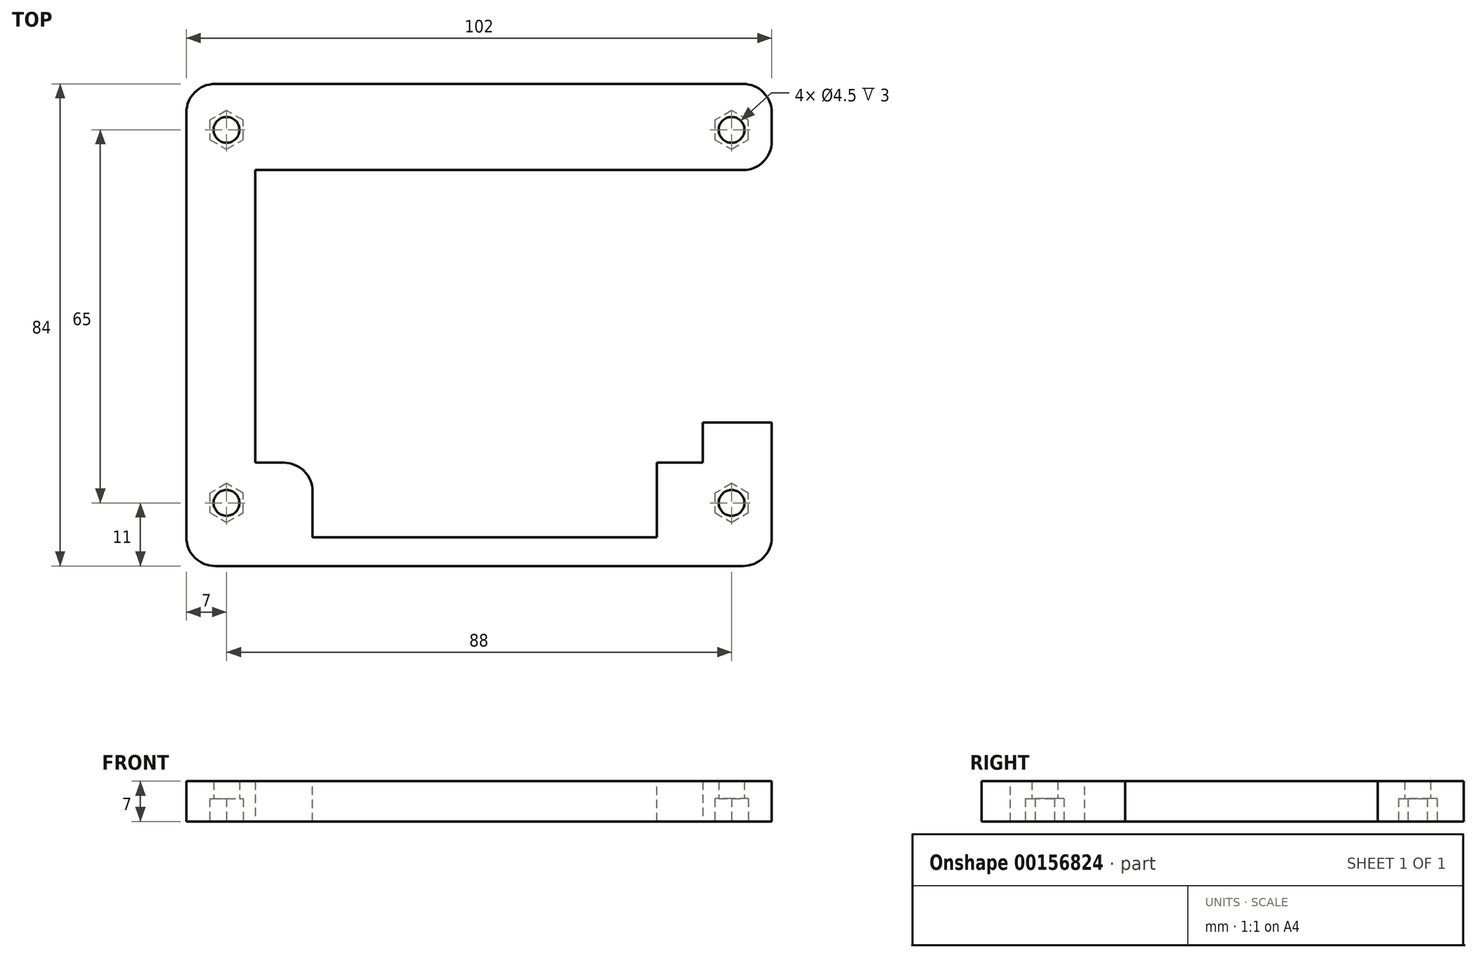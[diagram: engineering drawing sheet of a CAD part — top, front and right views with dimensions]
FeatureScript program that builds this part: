
annotation { "Feature Type Name" : "Feature", "Feature Type Description" : "" }
export const myFeature = defineFeature(function(context is Context, id is Id, definition is map)
    precondition{}
    {
        {
            var Q0;
            Q0=qCreatedBy(makeId("Top.planeOp"),FACE);
            var sketch = newSketch(context, id + "F0", { "sketchPlane" : qUnion([Q0])});
            skLineSegment(sketch, "E0.rect.bottom", {"start": v(44, -32.5) * mm, "end": v(-44, -32.5) * mm, "construction": true});
            skLineSegment(sketch, "E0.rect.top", {"start": v(44, 32.5) * mm, "end": v(-44, 32.5) * mm, "construction": true});
            skLineSegment(sketch, "E0.rect.left", {"start": v(44, -32.5) * mm, "end": v(44, 32.5) * mm, "construction": true});
            skLineSegment(sketch, "E0.rect.right", {"start": v(-44, -32.5) * mm, "end": v(-44, 32.5) * mm, "construction": true});
            skPoint(sketch, "E0.rect.middle", {"position": v(0, 0) * mm});
            skCircle(sketch, "E1", {"center": v(-44, 32.5) * mm, "radius": 2.25 * mm});
            skCircle(sketch, "E2", {"center": v(44, 32.5) * mm, "radius": 2.25 * mm});
            skCircle(sketch, "E3", {"center": v(-44, -32.5) * mm, "radius": 2.25 * mm});
            skCircle(sketch, "E4", {"center": v(44, -32.5) * mm, "radius": 2.25 * mm});
            skLineSegment(sketch, "E5.rect.bottom", {"start": v(39, -25.5) * mm, "end": v(-39, -25.5) * mm});
            skLineSegment(sketch, "E5.rect.top", {"start": v(39, 25.5) * mm, "end": v(-39, 25.5) * mm});
            skLineSegment(sketch, "E5.rect.left", {"start": v(39, -25.5) * mm, "end": v(39, 25.5) * mm});
            skLineSegment(sketch, "E5.rect.right", {"start": v(-39, -25.5) * mm, "end": v(-39, 25.5) * mm});
            skLineSegment(sketch, "E6", {"start": v(-51, -43.5) * mm, "end": v(51, -43.5) * mm});
            skLineSegment(sketch, "E7", {"start": v(51, -43.5) * mm, "end": v(51, 40.5) * mm});
            skLineSegment(sketch, "E8", {"start": v(51, 40.5) * mm, "end": v(-51, 40.5) * mm});
            skLineSegment(sketch, "E9", {"start": v(-51, 40.5) * mm, "end": v(-51, -43.5) * mm});
            skSolve(sketch);
        }
        {
            var Q0;
            Q0=qSketchRegion(id+"F0",true);
            extrude(context, id + "F1", {"entities" : qUnion([Q0]), "depth" : 15 * mm});
        }
        {
            var Q0;
            Q0=makeQuery(id+"F1.opExtrude","CAP_FACE",FACE,{"disambiguationData":[OSD([sQuery(id+"F0.wireOp",EDGE,"E1"),sQuery(id+"F0.wireOp",EDGE,"E2"),sQuery(id+"F0.wireOp",EDGE,"E3"),sQuery(id+"F0.wireOp",EDGE,"E4"),sQuery(id+"F0.wireOp",EDGE,"E5.rect.bottom"),sQuery(id+"F0.wireOp",EDGE,"E5.rect.top"),sQuery(id+"F0.wireOp",EDGE,"E5.rect.left"),sQuery(id+"F0.wireOp",EDGE,"E5.rect.right"),sQuery(id+"F0.wireOp",EDGE,"E6"),sQuery(id+"F0.wireOp",EDGE,"E7"),sQuery(id+"F0.wireOp",EDGE,"E8"),sQuery(id+"F0.wireOp",EDGE,"E9")])],"isStart":true});
            var sketch = newSketch(context, id + "F2", { "sketchPlane" : qUnion([Q0])});
            skCircle(sketch, "E10.cCircle", {"center": v(-44, 32.5) * mm, "radius": 2.92 * mm, "construction": true});
            skLineSegment(sketch, "E10.0", {"start": v(-41.08, 34.19) * mm, "end": v(-41.08, 30.81) * mm});
            skLineSegment(sketch, "E10.1", {"start": v(-41.08, 30.81) * mm, "end": v(-44, 29.12) * mm});
            skLineSegment(sketch, "E10.2", {"start": v(-44, 29.12) * mm, "end": v(-46.93, 30.81) * mm});
            skLineSegment(sketch, "E10.3", {"start": v(-46.93, 30.81) * mm, "end": v(-46.93, 34.19) * mm});
            skLineSegment(sketch, "E10.4", {"start": v(-46.93, 34.19) * mm, "end": v(-44, 35.88) * mm});
            skLineSegment(sketch, "E10.5", {"start": v(-44, 35.88) * mm, "end": v(-41.08, 34.19) * mm});
            skPoint(sketch, "E10.0.midPoint", {"position": v(-41.08, 32.5) * mm});
            skCircle(sketch, "E11.cCircle", {"center": v(44, 32.5) * mm, "radius": 2.92 * mm, "construction": true});
            skLineSegment(sketch, "E11.0", {"start": v(41.08, 30.81) * mm, "end": v(41.08, 34.19) * mm});
            skLineSegment(sketch, "E11.1", {"start": v(41.08, 34.19) * mm, "end": v(44, 35.88) * mm});
            skLineSegment(sketch, "E11.2", {"start": v(44, 35.88) * mm, "end": v(46.93, 34.19) * mm});
            skLineSegment(sketch, "E11.3", {"start": v(46.92, 34.19) * mm, "end": v(46.92, 30.81) * mm});
            skLineSegment(sketch, "E11.4", {"start": v(46.93, 30.81) * mm, "end": v(44, 29.12) * mm});
            skLineSegment(sketch, "E11.5", {"start": v(44, 29.12) * mm, "end": v(41.08, 30.81) * mm});
            skPoint(sketch, "E11.0.midPoint", {"position": v(41.08, 32.5) * mm});
            skCircle(sketch, "E12.cCircle", {"center": v(44, -32.5) * mm, "radius": 2.92 * mm, "construction": true});
            skLineSegment(sketch, "E12.0", {"start": v(41.08, -34.19) * mm, "end": v(41.08, -30.81) * mm});
            skLineSegment(sketch, "E12.1", {"start": v(41.08, -30.81) * mm, "end": v(44, -29.12) * mm});
            skLineSegment(sketch, "E12.2", {"start": v(44, -29.12) * mm, "end": v(46.93, -30.81) * mm});
            skLineSegment(sketch, "E12.3", {"start": v(46.93, -30.81) * mm, "end": v(46.93, -34.19) * mm});
            skLineSegment(sketch, "E12.4", {"start": v(46.93, -34.19) * mm, "end": v(44, -35.88) * mm});
            skLineSegment(sketch, "E12.5", {"start": v(44, -35.88) * mm, "end": v(41.08, -34.19) * mm});
            skPoint(sketch, "E12.0.midPoint", {"position": v(41.08, -32.5) * mm});
            skCircle(sketch, "E13.cCircle", {"center": v(-44, -32.5) * mm, "radius": 2.92 * mm, "construction": true});
            skLineSegment(sketch, "E13.0", {"start": v(-41.08, -30.81) * mm, "end": v(-41.08, -34.19) * mm});
            skLineSegment(sketch, "E13.1", {"start": v(-41.08, -34.19) * mm, "end": v(-44, -35.88) * mm});
            skLineSegment(sketch, "E13.2", {"start": v(-44, -35.88) * mm, "end": v(-46.93, -34.19) * mm});
            skLineSegment(sketch, "E13.3", {"start": v(-46.93, -34.19) * mm, "end": v(-46.93, -30.81) * mm});
            skLineSegment(sketch, "E13.4", {"start": v(-46.93, -30.81) * mm, "end": v(-44, -29.12) * mm});
            skLineSegment(sketch, "E13.5", {"start": v(-44, -29.12) * mm, "end": v(-41.08, -30.81) * mm});
            skPoint(sketch, "E13.0.midPoint", {"position": v(-41.08, -32.5) * mm});
            skSolve(sketch);
        }
        {
            var Q0;
            Q0=qSketchRegion(id+"F2",true);
            extrude(context, id + "F3", {"entities" : qUnion([Q0]), "operationType" : NewBodyOperationType.REMOVE, "oppositeDirection" : true, "depth" : 4 * mm});
        }
        {
            var Q0;
            Q0=makeQuery(id+"F1.opExtrude","CAP_FACE",FACE,{"disambiguationData":[OSD([sQuery(id+"F0.wireOp",EDGE,"E1"),sQuery(id+"F0.wireOp",EDGE,"E2"),sQuery(id+"F0.wireOp",EDGE,"E3"),sQuery(id+"F0.wireOp",EDGE,"E4"),sQuery(id+"F0.wireOp",EDGE,"E5.rect.bottom"),sQuery(id+"F0.wireOp",EDGE,"E5.rect.top"),sQuery(id+"F0.wireOp",EDGE,"E5.rect.left"),sQuery(id+"F0.wireOp",EDGE,"E5.rect.right"),sQuery(id+"F0.wireOp",EDGE,"E6"),sQuery(id+"F0.wireOp",EDGE,"E7"),sQuery(id+"F0.wireOp",EDGE,"E8"),sQuery(id+"F0.wireOp",EDGE,"E9")])],"isStart":false});
            var sketch = newSketch(context, id + "F4", { "sketchPlane" : qUnion([Q0])});
            skLineSegment(sketch, "E14", {"start": v(39, -18.5) * mm, "end": v(51, -18.5) * mm});
            skLineSegment(sketch, "E15", {"start": v(51, -18.5) * mm, "end": v(51, 25.5) * mm});
            skLineSegment(sketch, "E16", {"start": v(51, 25.5) * mm, "end": v(39, 25.5) * mm});
            skLineSegment(sketch, "E17", {"start": v(39, 25.5) * mm, "end": v(39, -18.5) * mm});
            skLineSegment(sketch, "E18", {"start": v(31, -25.5) * mm, "end": v(31, -38.5) * mm});
            skLineSegment(sketch, "E19", {"start": v(31, -38.5) * mm, "end": v(-29, -38.5) * mm});
            skLineSegment(sketch, "E20", {"start": v(-29, -38.5) * mm, "end": v(-29, -25.5) * mm});
            skLineSegment(sketch, "E21", {"start": v(-29, -25.5) * mm, "end": v(31, -25.5) * mm});
            skSolve(sketch);
        }
        {
            var Q0;
            Q0=qSketchRegion(id+"F4",true);
            extrude(context, id + "F5", {"entities" : qUnion([Q0]), "operationType" : NewBodyOperationType.REMOVE, "endBound" : BoundingType.THROUGH_ALL, "oppositeDirection" : true, "depth" : 5 * mm});
        }
        {
            var Q0;
            Q0=makeQuery(id+"F1.opExtrude","CAP_FACE",FACE,{"disambiguationData":[OSD([sQuery(id+"F0.wireOp",EDGE,"E1"),sQuery(id+"F0.wireOp",EDGE,"E2"),sQuery(id+"F0.wireOp",EDGE,"E3"),sQuery(id+"F0.wireOp",EDGE,"E4"),sQuery(id+"F0.wireOp",EDGE,"E5.rect.bottom"),sQuery(id+"F0.wireOp",EDGE,"E5.rect.top"),sQuery(id+"F0.wireOp",EDGE,"E5.rect.left"),sQuery(id+"F0.wireOp",EDGE,"E5.rect.right"),sQuery(id+"F0.wireOp",EDGE,"E6"),sQuery(id+"F0.wireOp",EDGE,"E7"),sQuery(id+"F0.wireOp",EDGE,"E8"),sQuery(id+"F0.wireOp",EDGE,"E9")])],"isStart":false});
            var sketch = newSketch(context, id + "F6", { "sketchPlane" : qUnion([Q0])});
            skLineSegment(sketch, "E22.rect.bottom", {"start": v(-51, 40.5) * mm, "end": v(51, 40.5) * mm});
            skLineSegment(sketch, "E22.rect.top", {"start": v(-51, -43.5) * mm, "end": v(51, -43.5) * mm});
            skLineSegment(sketch, "E22.rect.left", {"start": v(-51, 40.5) * mm, "end": v(-51, -43.5) * mm});
            skLineSegment(sketch, "E22.rect.right", {"start": v(51, 40.5) * mm, "end": v(51, -43.5) * mm});
            skPoint(sketch, "E22.rect.middle", {"position": v(0, -1.5) * mm});
            skSolve(sketch);
        }
        {
            var Q0;
            Q0=qSketchRegion(id+"F6",true);
            extrude(context, id + "F7", {"entities" : qUnion([Q0]), "operationType" : NewBodyOperationType.REMOVE, "oppositeDirection" : true, "depth" : 8 * mm});
        }
        {
            var Q0;
            Q0=makeQuery(id+"F1.opExtrude","SWEPT_EDGE",EDGE,{"disambiguationData":[OSD([sQuery(id+"F0.wireOp",EDGE,"E8"),sQuery(id+"F0.wireOp",EDGE,"E9")])]});
            var Q1;
            Q1=makeQuery(id+"F1.opExtrude","SWEPT_EDGE",EDGE,{"disambiguationData":[OSD([sQuery(id+"F0.wireOp",EDGE,"E7"),sQuery(id+"F0.wireOp",EDGE,"E8")])]});
            var Q2;
            Q2=makeQuery(id+"F1.opExtrude","SWEPT_EDGE",EDGE,{"disambiguationData":[OSD([sQuery(id+"F0.wireOp",EDGE,"E6"),sQuery(id+"F0.wireOp",EDGE,"E9")])]});
            var Q3;
            Q3=makeQuery(id+"F1.opExtrude","SWEPT_EDGE",EDGE,{"disambiguationData":[OSD([sQuery(id+"F0.wireOp",EDGE,"E6"),sQuery(id+"F0.wireOp",EDGE,"E7")])]});
            var Q4;
            Q4=makeQuery(id+"F5.boolean.opBoolean","COPY",EDGE,{"derivedFrom":makeQuery(id+"F5.opExtrude","SWEPT_EDGE",EDGE,{"disambiguationData":[OSD([sQuery(id+"F0.wireOp",EDGE,"E7"),sQuery(id+"F4.wireOp",EDGE,"E15"),sQuery(id+"F4.wireOp",EDGE,"E16")])]})});
            var Q5;
            Q5=makeQuery(id+"F5.boolean.opBoolean","COPY",EDGE,{"derivedFrom":makeQuery(id+"F5.opExtrude","SWEPT_EDGE",EDGE,{"disambiguationData":[OSD([sQuery(id+"F0.wireOp",EDGE,"E7"),sQuery(id+"F4.wireOp",EDGE,"E14"),sQuery(id+"F4.wireOp",EDGE,"E15")])]})});
            var Q6;
            Q6=makeQuery(id+"F5.boolean.opBoolean","COPY",EDGE,{"derivedFrom":makeQuery(id+"F5.opExtrude","SWEPT_EDGE",EDGE,{"disambiguationData":[OSD([sQuery(id+"F0.wireOp",EDGE,"E5.rect.left"),sQuery(id+"F4.wireOp",EDGE,"E16"),sQuery(id+"F4.wireOp",EDGE,"E17")])]})});
            var Q7;
            Q7=makeQuery(id+"F5.boolean.opBoolean","COPY",EDGE,{"derivedFrom":makeQuery(id+"F5.opExtrude","SWEPT_EDGE",EDGE,{"disambiguationData":[OSD([sQuery(id+"F0.wireOp",EDGE,"E5.rect.left"),sQuery(id+"F4.wireOp",EDGE,"E14"),sQuery(id+"F4.wireOp",EDGE,"E17")])]})});
            var Q8;
            Q8=makeQuery(id+"F5.boolean.opBoolean","COPY",EDGE,{"derivedFrom":makeQuery(id+"F5.opExtrude","SWEPT_EDGE",EDGE,{"disambiguationData":[OSD([sQuery(id+"F0.wireOp",EDGE,"E5.rect.bottom"),sQuery(id+"F4.wireOp",EDGE,"E18"),sQuery(id+"F4.wireOp",EDGE,"E21")])]})});
            var Q9;
            Q9=makeQuery(id+"F5.boolean.opBoolean","COPY",EDGE,{"derivedFrom":makeQuery(id+"F5.opExtrude","SWEPT_EDGE",EDGE,{"disambiguationData":[OSD([sQuery(id+"F0.wireOp",EDGE,"E5.rect.bottom"),sQuery(id+"F4.wireOp",EDGE,"E20"),sQuery(id+"F4.wireOp",EDGE,"E21")])]})});
            fillet(context, id + "F8", {"entities" : qUnion([Q0, Q1, Q2, Q3, Q4, Q5, Q6, Q7, Q8, Q9]), "radius" : 5 * mm, "tangentPropagation" : true, "allowEdgeOverflow" : false});
        }
    });
